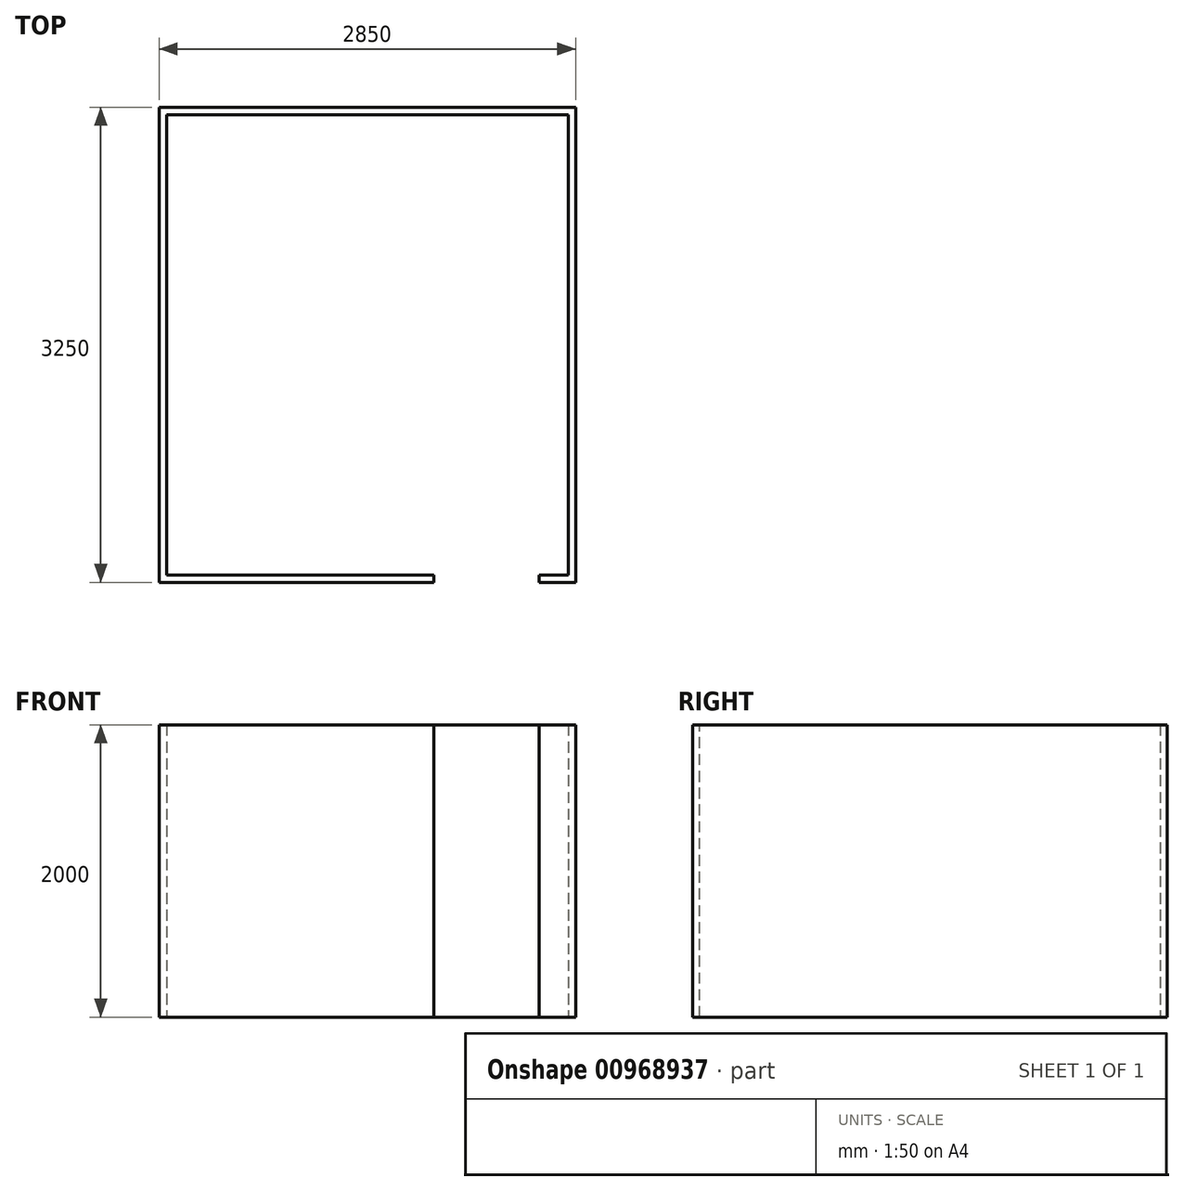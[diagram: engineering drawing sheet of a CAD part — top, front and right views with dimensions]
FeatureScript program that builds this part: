
annotation { "Feature Type Name" : "Feature", "Feature Type Description" : "" }
export const myFeature = defineFeature(function(context is Context, id is Id, definition is map)
    precondition{}
    {
        {
            var Q0;
            Q0=qCreatedBy(makeId("Top.planeOp"),FACE);
            var sketch = newSketch(context, id + "F0", { "sketchPlane" : qUnion([Q0])});
            skLineSegment(sketch, "E0.bottom", {"start": v(1425, 1625) * mm, "end": v(-1425, 1625) * mm});
            skLineSegment(sketch, "E0.top", {"start": v(1425, -1625) * mm, "end": v(-1425, -1625) * mm});
            skLineSegment(sketch, "E0.left", {"start": v(1425, 1625) * mm, "end": v(1425, -1625) * mm});
            skLineSegment(sketch, "E0.right", {"start": v(-1425, 1625) * mm, "end": v(-1425, -1625) * mm});
            skPoint(sketch, "E0.middle", {"position": v(0, 0) * mm});
            skLineSegment(sketch, "E1.0", {"start": v(-1375, 1575) * mm, "end": v(-1375, -1575) * mm});
            skLineSegment(sketch, "E1.1", {"start": v(1375, 1575) * mm, "end": v(-1375, 1575) * mm});
            skLineSegment(sketch, "E1.2", {"start": v(1375, 1575) * mm, "end": v(1375, -1575) * mm});
            skLineSegment(sketch, "E1.3", {"start": v(1375, -1575) * mm, "end": v(-1375, -1575) * mm});
            skSolve(sketch);
        }
        {
            var Q0;
            Q0 = qSketchRegion(id + "F0", true);
            extrude(context, id + "F1", {"entities" : qUnion([Q0]), "depth" : 2000 * mm, "offsetDistance" : 25 * mm});
        }
        {
            var Q0;
            Q0=makeQuery(id+"F1.opExtrude","CAP_FACE",FACE,{"disambiguationData":[OSD([sQuery(id+"F0.wireOp",EDGE,"E0.bottom"),sQuery(id+"F0.wireOp",EDGE,"E0.top"),sQuery(id+"F0.wireOp",EDGE,"E0.left"),sQuery(id+"F0.wireOp",EDGE,"E0.right"),sQuery(id+"F0.wireOp",EDGE,"E1.0"),sQuery(id+"F0.wireOp",EDGE,"E1.1"),sQuery(id+"F0.wireOp",EDGE,"E1.2"),sQuery(id+"F0.wireOp",EDGE,"E1.3")])],"isStart":false});
            var sketch = newSketch(context, id + "F2", { "sketchPlane" : qUnion([Q0])});
            skPoint(sketch, "E2", {"position": v(1175, -1625) * mm});
            skPoint(sketch, "E3", {"position": v(455, -1625) * mm});
            skLineSegment(sketch, "E4.bottom", {"start": v(455, -1625) * mm, "end": v(1175, -1625) * mm});
            skLineSegment(sketch, "E4.top", {"start": v(455, -1575) * mm, "end": v(1175, -1575) * mm});
            skLineSegment(sketch, "E4.left", {"start": v(455, -1625) * mm, "end": v(455, -1575) * mm});
            skLineSegment(sketch, "E4.right", {"start": v(1175, -1625) * mm, "end": v(1175, -1575) * mm});
            skSolve(sketch);
        }
        {
            var Q0;
            Q0 = qSketchRegion(id + "F2", true);
            extrude(context, id + "F3", {"entities" : qUnion([Q0]), "operationType" : NewBodyOperationType.REMOVE, "endBound" : BoundingType.UP_TO_NEXT, "oppositeDirection" : true, "depth" : 25 * mm, "offsetDistance" : 25 * mm});
        }
    });
